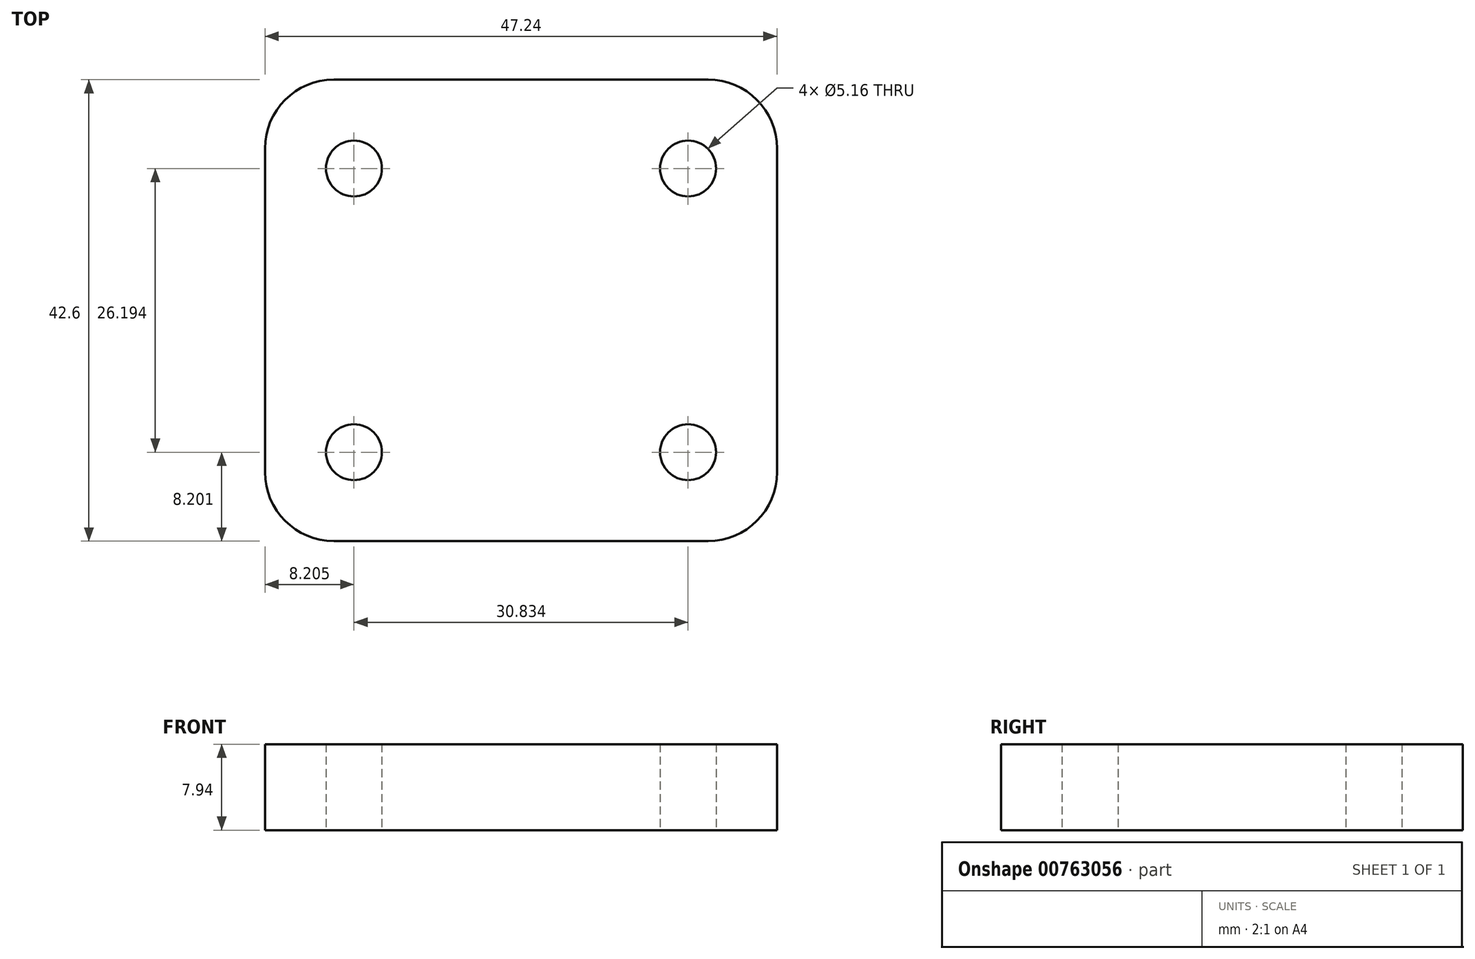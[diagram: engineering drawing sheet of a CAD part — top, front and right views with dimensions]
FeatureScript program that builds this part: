
annotation { "Feature Type Name" : "Feature", "Feature Type Description" : "" }
export const myFeature = defineFeature(function(context is Context, id is Id, definition is map)
    precondition{}
    {
        {
            var Q0;
            Q0=qCreatedBy(makeId("Top.planeOp"),FACE);
            var sketch = newSketch(context, id + "F0", { "sketchPlane" : qUnion([Q0])});
            skLineSegment(sketch, "E0.bottom", {"start": v(6.35, 0) * mm, "end": v(40.9, 0) * mm});
            skLineSegment(sketch, "E0.top", {"start": v(6.35, 42.6) * mm, "end": v(40.9, 42.6) * mm});
            skLineSegment(sketch, "E0.left", {"start": v(0, 6.35) * mm, "end": v(0, 36.25) * mm});
            skLineSegment(sketch, "E0.right", {"start": v(47.24, 6.35) * mm, "end": v(47.24, 36.25) * mm});
            skCircle(sketch, "E1", {"center": v(8.2, 8.2) * mm, "radius": 2.58 * mm});
            skCircle(sketch, "E2.0.1.0", {"center": v(8.2, 34.4) * mm, "radius": 2.58 * mm});
            skCircle(sketch, "E2.1.0.0", {"center": v(39.04, 8.2) * mm, "radius": 2.58 * mm});
            skCircle(sketch, "E2.1.1.0", {"center": v(39.04, 34.4) * mm, "radius": 2.58 * mm});
            skLineSegment(sketch, "E2.direction1", {"start": v(8.2, 8.2) * mm, "end": v(39.04, 8.2) * mm, "construction": true});
            skLineSegment(sketch, "E2.direction2", {"start": v(8.2, 8.2) * mm, "end": v(8.2, 34.4) * mm, "construction": true});
            skPoint(sketch, "E3.visualSharp", {"position": v(47.24, 42.6) * mm});
            skArc(sketch, "E3.filletArc", {"start": v(47.24, 36.25) * mm, "mid": v(45.38, 40.74) * mm, "end": v(40.9, 42.6) * mm});
            skPoint(sketch, "E4.visualSharp", {"position": v(0, 42.6) * mm});
            skArc(sketch, "E4.filletArc", {"start": v(6.35, 42.6) * mm, "mid": v(1.86, 40.74) * mm, "end": v(0, 36.25) * mm});
            skPoint(sketch, "E5.visualSharp", {"position": v(47.24, 0) * mm});
            skArc(sketch, "E5.filletArc", {"start": v(40.9, 0) * mm, "mid": v(45.38, 1.86) * mm, "end": v(47.24, 6.35) * mm});
            skPoint(sketch, "E6.visualSharp", {"position": v(0, 0) * mm});
            skArc(sketch, "E6.filletArc", {"start": v(0, 6.35) * mm, "mid": v(1.86, 1.86) * mm, "end": v(6.35, 0) * mm});
            skSolve(sketch);
        }
        {
            var Q0;
            Q0 = qSketchRegion(id + "F0", true);
            extrude(context, id + "F1", {"entities" : qUnion([Q0]), "depth" : 7.94 * mm, "offsetDistance" : 25.4 * mm});
        }
    });
